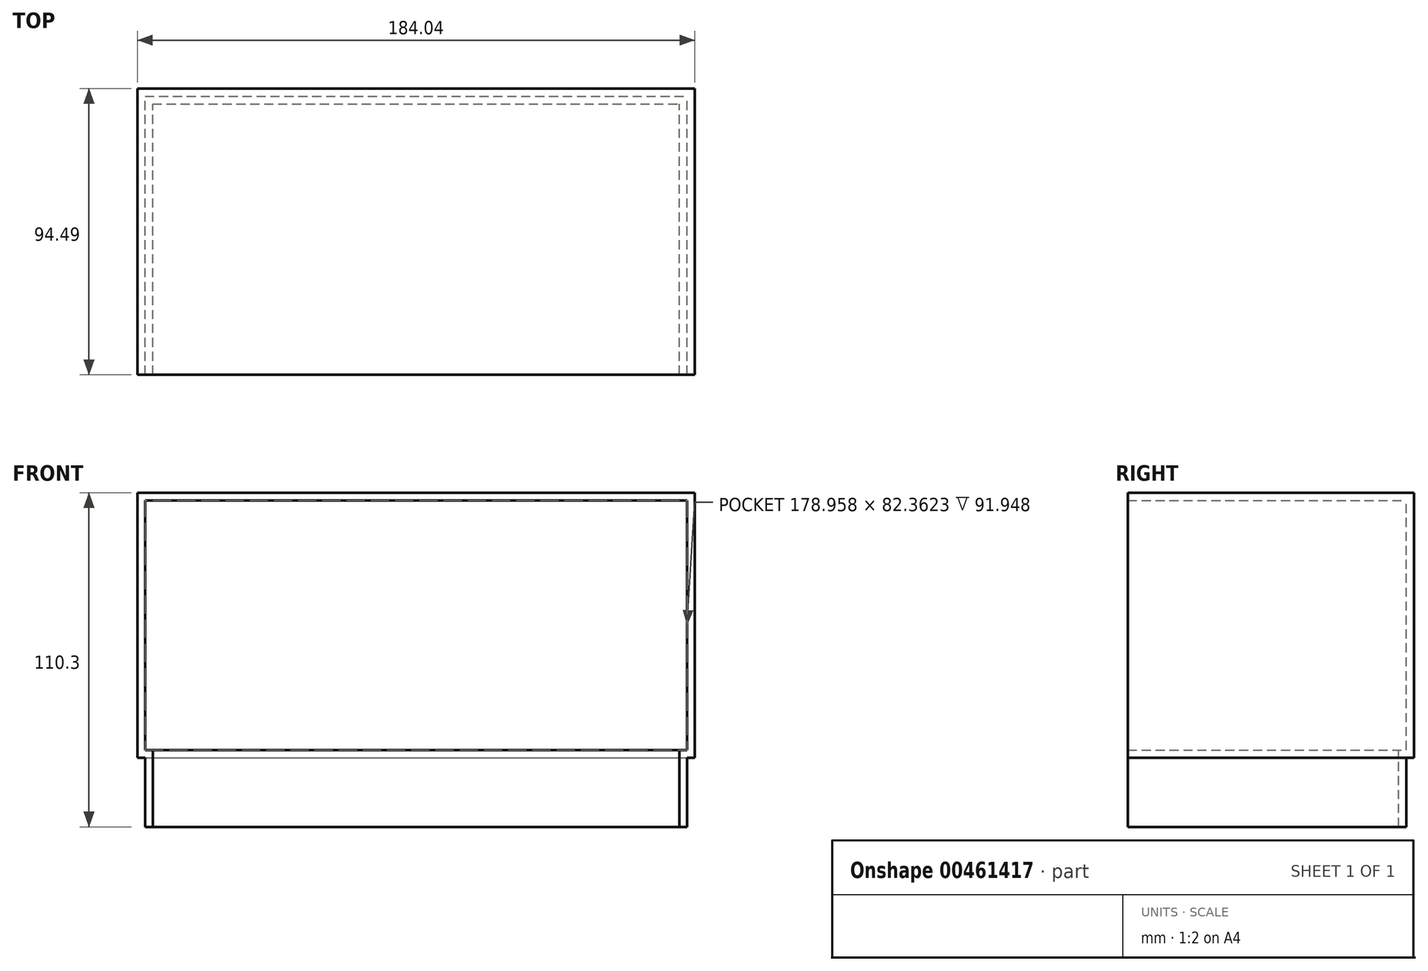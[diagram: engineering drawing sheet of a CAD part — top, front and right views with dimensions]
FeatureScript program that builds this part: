
annotation { "Feature Type Name" : "Feature", "Feature Type Description" : "" }
export const myFeature = defineFeature(function(context is Context, id is Id, definition is map)
    precondition{}
    {
        {
            var Q0;
            Q0=qCreatedBy(makeId("Front.planeOp"),FACE);
            var sketch = newSketch(context, id + "F0", { "sketchPlane" : qUnion([Q0])});
            skLineSegment(sketch, "E0.bottom", {"start": v(-19.3, 0) * mm, "end": v(164.75, 0) * mm});
            skLineSegment(sketch, "E0.top", {"start": v(-19.3, 87.44) * mm, "end": v(164.75, 87.44) * mm});
            skLineSegment(sketch, "E0.left", {"start": v(-19.3, 0) * mm, "end": v(-19.3, 87.44) * mm});
            skLineSegment(sketch, "E0.right", {"start": v(164.75, 0) * mm, "end": v(164.75, 87.44) * mm});
            skSolve(sketch);
        }
        {
            var Q0;
            Q0 = qSketchRegion(id + "F0", true);
            extrude(context, id + "F1", {"entities" : qUnion([Q0]), "depth" : 94.49 * mm});
        }
        {
            var Q0;
            Q0=makeQuery(id+"F1.opExtrude","CAP_FACE",FACE,{"disambiguationData":[OSD([sQuery(id+"F0.wireOp",EDGE,"E0.bottom"),sQuery(id+"F0.wireOp",EDGE,"E0.top"),sQuery(id+"F0.wireOp",EDGE,"E0.left"),sQuery(id+"F0.wireOp",EDGE,"E0.right")])],"isStart":false});
            shell(context, id + "F2", {"entities" : qUnion([Q0]), "thickness" : 2.54 * mm});
        }
        {
            var Q0;
            Q0=makeQuery(id+"F2.opShell","OFFSET_FACE",FACE,{"disambiguationData":[OSD([sQuery(id+"F0.wireOp",EDGE,"E0.bottom")])]});
            extrude(context, id + "F3", {"entities" : qUnion([Q0]), "operationType" : NewBodyOperationType.ADD, "oppositeDirection" : true, "depth" : 25.4 * mm});
        }
        {
            var Q0;
            Q0=makeQuery(id+"F2.opShell","OFFSET_FACE",FACE,{"disambiguationData":[OSD([sQuery(id+"F0.wireOp",EDGE,"E0.bottom")])]});
            var Q1;
            Q1=makeQuery(id+"F3.opExtrude","CAP_FACE",FACE,{"disambiguationData":[OSD([sQuery(id+"F0.wireOp",EDGE,"E0.bottom")])],"isStart":false});
            var Q2;
            {var subQ0=sQuery(id+"F0.wireOp",EDGE,"E0.bottom");Q2=makeQuery(id+"F3.boolean.opBoolean","MERGE",FACE,{"derivedFrom":[makeQuery(id+"F1.opExtrude","CAP_FACE",FACE,{"disambiguationData":[OSD([subQ0,sQuery(id+"F0.wireOp",EDGE,"E0.top"),sQuery(id+"F0.wireOp",EDGE,"E0.left"),sQuery(id+"F0.wireOp",EDGE,"E0.right")])],"isStart":false}),makeQuery(id+"F3.opExtrude","SWEPT_FACE",FACE,{"disambiguationData":[OSD([subQ0]),TDD([makeQuery(id+"F2.opShell","OFFSET_EDGE",EDGE,{"disambiguationData":[OSD([subQ0]),TDD([makeQuery(id+"F1.opExtrude","CAP_EDGE",EDGE,{"disambiguationData":[OSD([subQ0])],"isStart":false})])]})])]})]});}
            shell(context, id + "F4", {"entities" : qUnion([Q0, Q1, Q2]), "thickness" : 2.54 * mm});
        }
    });
